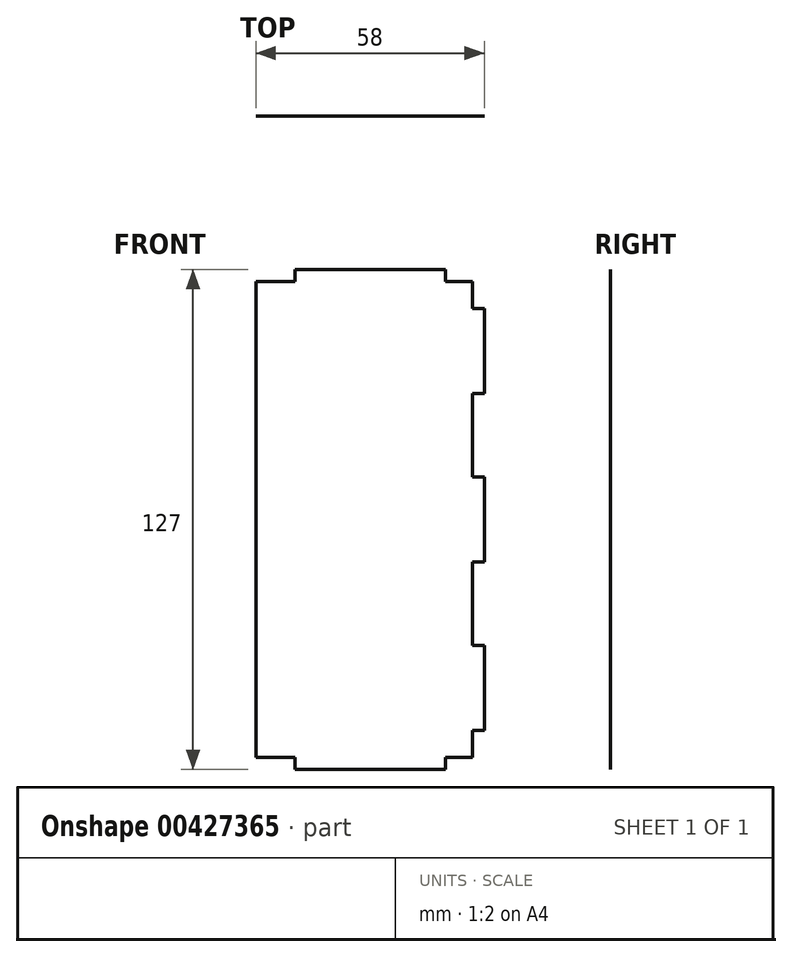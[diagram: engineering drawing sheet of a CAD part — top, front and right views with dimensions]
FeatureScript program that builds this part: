
annotation { "Feature Type Name" : "Feature", "Feature Type Description" : "" }
export const myFeature = defineFeature(function(context is Context, id is Id, definition is map)
    precondition{}
    {
        {
            var Q0;
            Q0=qCreatedBy(makeId("Front.planeOp"),FACE);
            var sketch = newSketch(context, id + "F0", { "sketchPlane" : qUnion([Q0])});
            skLineSegment(sketch, "E0.bottom", {"start": v(29, 63.5) * mm, "end": v(-29, 63.5) * mm});
            skLineSegment(sketch, "E0.top", {"start": v(29, -63.5) * mm, "end": v(-29, -63.5) * mm});
            skLineSegment(sketch, "E0.left", {"start": v(29, 63.5) * mm, "end": v(29, -63.5) * mm});
            skLineSegment(sketch, "E0.right", {"start": v(-29, 63.5) * mm, "end": v(-29, -63.5) * mm});
            skPoint(sketch, "E0.middle", {"position": v(0, 0) * mm});
            skSolve(sketch);
        }
        {
            var Q0;
            Q0=makeQuery(id+"F0.imprint","IMPRINT",FACE,{"disambiguationData":[TD([[makeQuery(id+"F0.imprint","IMPRINT",EDGE,{"derivedFrom":sQuery(id+"F0.wireOp",EDGE,"E0.bottom")}),1.0]])]});
            extrude(context, id + "F1", {"entities" : qUnion([Q0]), "depth" : 1 / 203.2 * mm, "offsetDistance" : 25 * mm});
        }
        {
            var Q0;
            Q0=makeQuery(id+"F1.opExtrude","CAP_FACE",FACE,{"disambiguationData":[OSD([sQuery(id+"F0.wireOp",EDGE,"E0.bottom"),sQuery(id+"F0.wireOp",EDGE,"E0.top"),sQuery(id+"F0.wireOp",EDGE,"E0.left"),sQuery(id+"F0.wireOp",EDGE,"E0.right")])],"isStart":true});
            var sketch = newSketch(context, id + "F2", { "sketchPlane" : qUnion([Q0])});
            skLineSegment(sketch, "E1.bottom", {"start": v(-29, 63.5) * mm, "end": v(29, 63.5) * mm, "construction": true});
            skLineSegment(sketch, "E1.top", {"start": v(-29, -63.5) * mm, "end": v(29, -63.5) * mm, "construction": true});
            skLineSegment(sketch, "E1.left", {"start": v(-29, 63.5) * mm, "end": v(-29, -63.5) * mm, "construction": true});
            skLineSegment(sketch, "E1.right", {"start": v(29, 63.5) * mm, "end": v(29, -63.5) * mm, "construction": true});
            skPoint(sketch, "E1.middle", {"position": v(0, 0) * mm});
            skLineSegment(sketch, "E2.0", {"start": v(-29, 60.42) * mm, "end": v(25.93, 60.42) * mm, "construction": true});
            skLineSegment(sketch, "E2.2", {"start": v(-29, -60.42) * mm, "end": v(25.93, -60.42) * mm, "construction": true});
            skLineSegment(sketch, "E2.3", {"start": v(25.93, 60.42) * mm, "end": v(25.93, -60.42) * mm, "construction": true});
            skLineSegment(sketch, "E3.0", {"start": v(-34, -68.5) * mm, "end": v(34, -68.5) * mm, "construction": true});
            skLineSegment(sketch, "E3.1", {"start": v(-34, 68.5) * mm, "end": v(-34, -68.5) * mm, "construction": true});
            skLineSegment(sketch, "E3.2", {"start": v(34, 68.5) * mm, "end": v(-34, 68.5) * mm, "construction": true});
            skLineSegment(sketch, "E3.3", {"start": v(34, -68.5) * mm, "end": v(34, 68.5) * mm, "construction": true});
            skLineSegment(sketch, "E4", {"start": v(29, 53.5) * mm, "end": v(-29, 53.5) * mm, "construction": true});
            skLineSegment(sketch, "E5", {"start": v(-29, -53.5) * mm, "end": v(29, -53.5) * mm, "construction": true});
            skLineSegment(sketch, "E6", {"start": v(-29, 32.1) * mm, "end": v(29, 32.1) * mm, "construction": true});
            skLineSegment(sketch, "E7", {"start": v(-29, 10.7) * mm, "end": v(29, 10.7) * mm, "construction": true});
            skLineSegment(sketch, "E8", {"start": v(-29, -10.7) * mm, "end": v(29, -10.7) * mm, "construction": true});
            skLineSegment(sketch, "E9", {"start": v(-29, -32.1) * mm, "end": v(29, -32.1) * mm, "construction": true});
            skLineSegment(sketch, "E10", {"start": v(-25.92, 63.5) * mm, "end": v(-25.93, -63.5) * mm, "construction": true});
            skLineSegment(sketch, "E11", {"start": v(-23, 53.5) * mm, "end": v(-23, 32.1) * mm, "construction": true});
            skLineSegment(sketch, "E12", {"start": v(-23, 32.1) * mm, "end": v(-23, 10.7) * mm, "construction": true});
            skLineSegment(sketch, "E13", {"start": v(-23, 10.7) * mm, "end": v(-23, -10.7) * mm, "construction": true});
            skLineSegment(sketch, "E14", {"start": v(-23, -10.7) * mm, "end": v(-23, -32.1) * mm, "construction": true});
            skLineSegment(sketch, "E15", {"start": v(-19, 63.5) * mm, "end": v(-19, -63.5) * mm, "construction": true});
            skLineSegment(sketch, "E16", {"start": v(-29, 63.5) * mm, "end": v(-29, 53.6) * mm});
            skLineSegment(sketch, "E17", {"start": v(-29, 53.6) * mm, "end": v(-25.92, 53.6) * mm});
            skLineSegment(sketch, "E18", {"start": v(-25.92, 53.6) * mm, "end": v(-25.92, 60.42) * mm});
            skLineSegment(sketch, "E19", {"start": v(-25.92, 60.42) * mm, "end": v(-19.1, 60.42) * mm});
            skLineSegment(sketch, "E20", {"start": v(-19.1, 60.42) * mm, "end": v(-19.1, 63.5) * mm});
            skLineSegment(sketch, "E21", {"start": v(-19.1, 63.5) * mm, "end": v(-29, 63.5) * mm});
            skLineSegment(sketch, "E22", {"start": v(-23, -32.1) * mm, "end": v(-23, -53.5) * mm, "construction": true});
            skLineSegment(sketch, "E23.bottom", {"start": v(-29, 32) * mm, "end": v(-25.93, 32) * mm});
            skLineSegment(sketch, "E23.top", {"start": v(-29, 10.8) * mm, "end": v(-25.93, 10.8) * mm});
            skLineSegment(sketch, "E23.left", {"start": v(-29, 32) * mm, "end": v(-29, 10.8) * mm});
            skLineSegment(sketch, "E23.right", {"start": v(-25.93, 32) * mm, "end": v(-25.93, 10.8) * mm});
            skLineSegment(sketch, "E24.bottom", {"start": v(-29, -10.8) * mm, "end": v(-25.93, -10.8) * mm});
            skLineSegment(sketch, "E24.top", {"start": v(-29, -32) * mm, "end": v(-25.93, -32) * mm});
            skLineSegment(sketch, "E24.left", {"start": v(-29, -10.8) * mm, "end": v(-29, -32) * mm});
            skLineSegment(sketch, "E24.right", {"start": v(-25.93, -10.8) * mm, "end": v(-25.93, -32) * mm});
            skLineSegment(sketch, "E25", {"start": v(-29, -53.6) * mm, "end": v(-25.93, -53.6) * mm});
            skLineSegment(sketch, "E26", {"start": v(-25.93, -53.6) * mm, "end": v(-25.93, -60.42) * mm});
            skLineSegment(sketch, "E27", {"start": v(-25.93, -60.42) * mm, "end": v(-19.1, -60.42) * mm});
            skLineSegment(sketch, "E28", {"start": v(-19.1, -60.42) * mm, "end": v(-19.1, -63.5) * mm});
            skLineSegment(sketch, "E29", {"start": v(-19.1, -63.5) * mm, "end": v(-29, -63.5) * mm});
            skLineSegment(sketch, "E30", {"start": v(-29, -53.6) * mm, "end": v(-29, -63.5) * mm});
            skLineSegment(sketch, "E31", {"start": v(19, 63.5) * mm, "end": v(19, -63.5) * mm, "construction": true});
            skLineSegment(sketch, "E32", {"start": v(19.1, 63.5) * mm, "end": v(19.1, 60.42) * mm});
            skLineSegment(sketch, "E33", {"start": v(19.1, 60.43) * mm, "end": v(29, 60.43) * mm});
            skLineSegment(sketch, "E34", {"start": v(29, 60.42) * mm, "end": v(29, 63.5) * mm});
            skLineSegment(sketch, "E35", {"start": v(19.1, 63.5) * mm, "end": v(29, 63.5) * mm});
            skLineSegment(sketch, "E36", {"start": v(19.1, -63.5) * mm, "end": v(19.1, -60.42) * mm});
            skLineSegment(sketch, "E37", {"start": v(19.1, -60.42) * mm, "end": v(29, -60.42) * mm});
            skLineSegment(sketch, "E38", {"start": v(29, -60.42) * mm, "end": v(29, -63.5) * mm});
            skLineSegment(sketch, "E39", {"start": v(19.1, -63.5) * mm, "end": v(29, -63.5) * mm});
            skSolve(sketch);
        }
        {
            var Q0;
            Q0 = qSketchRegion(id + "F2", true);
            extrude(context, id + "F3", {"entities" : qUnion([Q0]), "operationType" : NewBodyOperationType.REMOVE, "oppositeDirection" : true, "depth" : 25 * mm, "offsetDistance" : 25 * mm});
        }
    });
